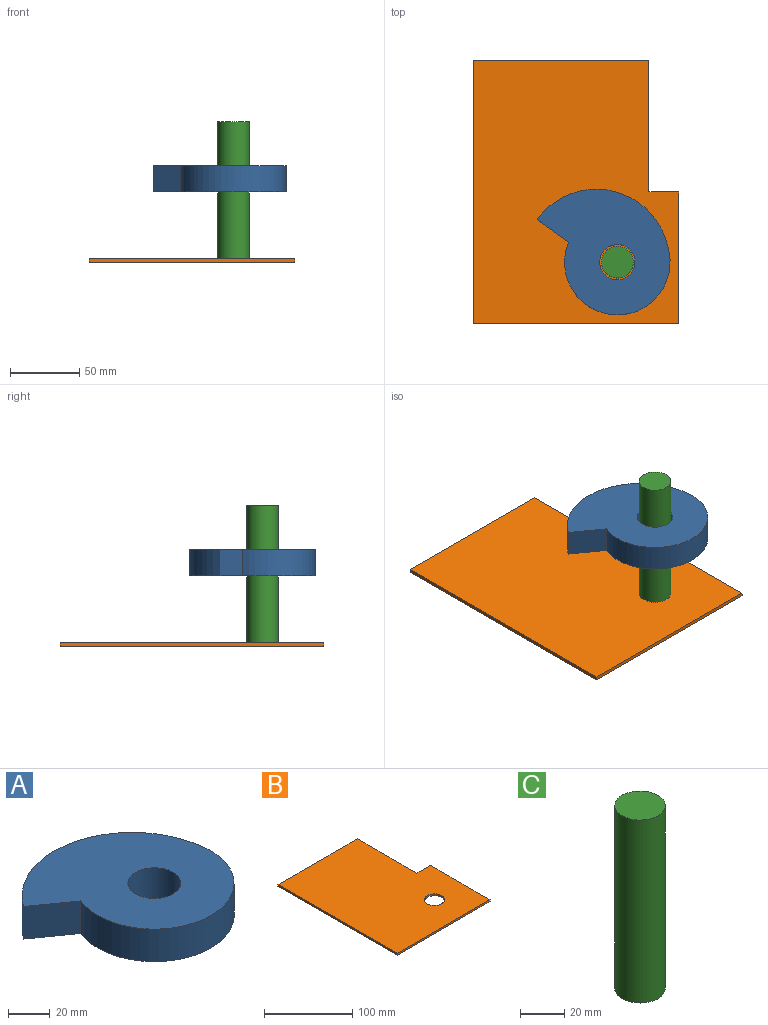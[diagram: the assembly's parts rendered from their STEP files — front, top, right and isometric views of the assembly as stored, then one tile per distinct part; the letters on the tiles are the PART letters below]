
ASSEMBLY  parts=3 mates=2
PART A: 6 faces, bbox 96.1x90.8x19.1 mm
  f0: cylinder r=52.71mm len=94.49mm, axis (0,0,-1), area 2321.9mm2, adj f1,f2,f3,f4
  f1: plane 22.73x19.05mm, normal (-0.58,-0.81,0), area 531.7mm2, adj f0,f2,f3,f4
  f2: cylinder r=38.1mm len=76.2mm, axis (0,0,-1), area 2774.1mm2, adj f0,f1,f3,f4
  f3: plane 96.11x90.81mm, normal (0,0,1), area 5454.4mm2, adj f0,f1,f2,f5
  f4: plane 96.11x90.81mm, normal (0,0,-1), area 5454.4mm2, adj f0,f1,f2,f5
  f5: cylinder r=12.7mm len=25.4mm, axis (0,0,1), area 1520.1mm2, adj f3,f4
PART B: 9 faces, bbox 148.6x190.5x2.5 mm
  f0: plane 148.61x2.54mm, normal (0,-1,0), area 377.5mm2, adj f3,f4,f5,f6
  f1: plane 95.25x2.54mm, normal (1,0,0), area 241.9mm2, adj f2,f4,f5,f7
  f2: plane 127x2.54mm, normal (0,1,0), area 322.6mm2, adj f1,f3,f4,f5
  f3: plane 190.5x2.54mm, normal (-1,0,0), area 483.9mm2, adj f0,f2,f4,f5
  f4: plane 190.5x148.61mm, normal (0,0,1), area 25841mm2, adj f0,f1,f2,f3,f6,f7,f8
  f5: plane 190.5x148.61mm, normal (0,0,-1), area 25841mm2, adj f0,f1,f2,f3,f6,f7,f8
  f6: plane 95.25x2.54mm, normal (1,0,0), area 241.9mm2, adj f0,f4,f5,f7
  f7: plane 21.61x2.54mm, normal (0,1,0), area 54.9mm2, adj f1,f4,f5,f6
  f8: cylinder r=11.43mm len=22.86mm, axis (0,0,1), area 182.4mm2, adj f4,f5
PART C: 3 faces, bbox 22.9x22.9x101.6 mm
  f0: cylinder r=11.43mm len=101.6mm, axis (0,0,-1), area 7296.6mm2, adj f1,f2
  f1: plane 22.86x22.86mm, normal (0,0,1), area 410.4mm2, adj f0
  f2: plane 22.86x22.86mm, normal (0,0,-1), area 410.4mm2, adj f0
PLACE A t=(-33.53,260.85,-163.8)mm
PLACE B t=(-74.19,311.65,-214.6)mm
PLACE C t=(-33.53,260.85,-214.6)mm
MATE revolute A.f2 <-> C.f0  axis (0,0,-1) through (-33.53,260.85,-163.8)mm
MATE fastened C.f0 <-> B.f8  axis (0,0,-1) through (-33.53,260.85,-214.6)mm
